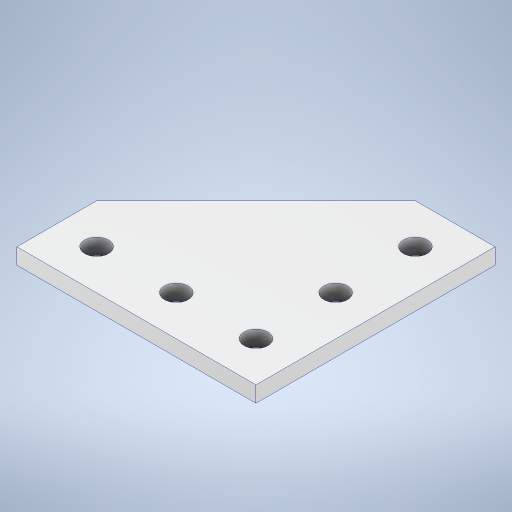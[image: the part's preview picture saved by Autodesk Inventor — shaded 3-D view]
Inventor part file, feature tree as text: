
AUTODESK INVENTOR PART (.ipt)
format: ipt  version: 2024 (Build 280153000, 153)  size: 254,976 bytes
history: native  units: in
note: dims shown in document units (in); Inventor stores cm internally (conversion verified against a paired STEP export)
features: extrude x1, sketch x1
ambient origin geometry x8: Origin, YZ Plane, XZ Plane, XY Plane, X Axis, Y Axis, Z Axis, Center Point
bodies: Solid1 (feature_tree)
feature tree (2):
  extrude  "Extrusion1"  Depth=3.0in
  sketch  "Sketch1"  dims[d0=1.0in d1=3.0in d2=3.0in d3=1.0in d4=1.0in d5=1.0in d6=1.0in d7=1.0in d8=0.3in d9=0.3in d10=0.3in d11=0.3in d12=0.3in d13=0.2in d14=0.0in]
